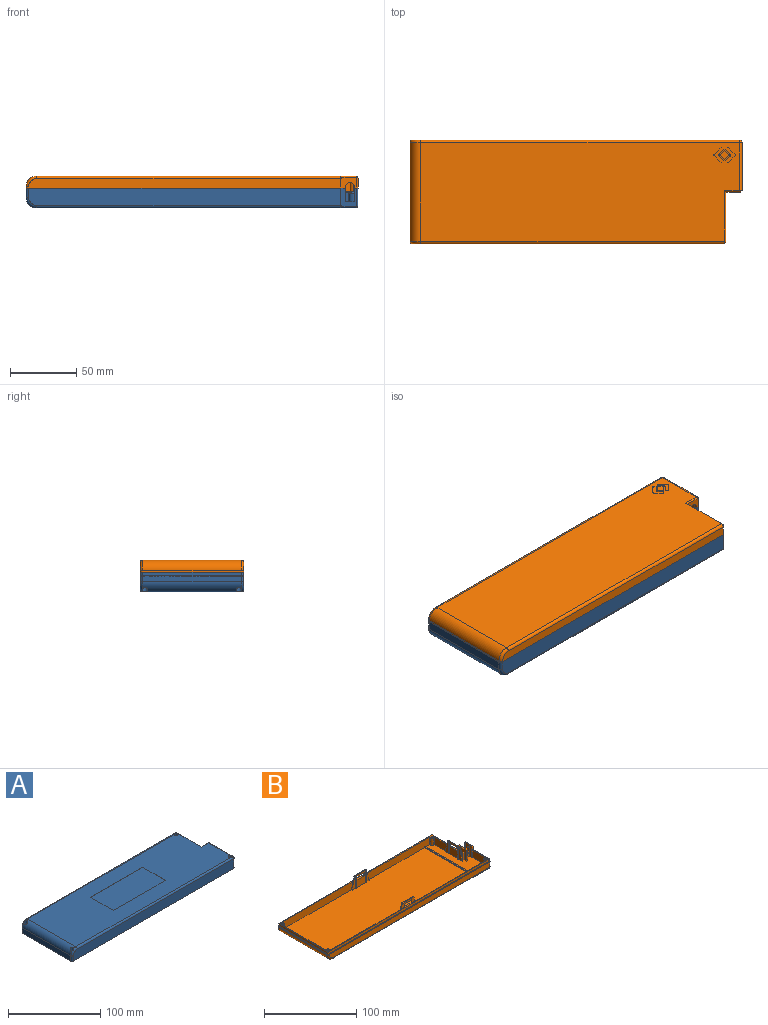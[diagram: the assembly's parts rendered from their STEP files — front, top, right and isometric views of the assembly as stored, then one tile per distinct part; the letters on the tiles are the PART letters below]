
ASSEMBLY  parts=2 mates=1
PART A: 171 faces, bbox 250.8x78.1x15.8 mm
  f0: plane 74x22.5mm, normal (0,0,-1), area 1104.2mm2, adj f1,f2,f3,f4,f12,f13,f18,f19
  f1: plane 20.61x10.11mm, normal (-1,0,0), area 193.9mm2, adj f0,f17,f131,f133,f160,f161
  f2: plane 58.61x10.11mm, normal (0,1,0), area 572.4mm2, adj f0,f17,f29,f30,f31,f40,f128,f160
  f3: plane 35.61x10.11mm, normal (-1,0,0), area 328.9mm2, adj f0,f17,f120,f148,f149,f152,f159,f162
  f4: plane 46.51x10.11mm, normal (0,-1,0), area 451.4mm2, adj f0,f17,f29,f30,f31,f60,f128,f159
  f5: plane 67.11x4.11mm, normal (1,0,0), area 259.8mm2, adj f17,f115,f157,f158,f163,f164
  f6: plane 1.5x1.29mm, normal (1,0,0), area 1.1mm2, adj f126,f147,f150,f168
  f7: plane 1.5x1.29mm, normal (-1,0,0), area 1.1mm2, adj f126,f147,f150,f168
  f8: plane 10x1.2mm, normal (0,0,1), area 12mm2, adj f9,f78,f79,f167
  f9: plane 38x10mm, normal (0,1,0), area 365mm2, adj f8,f17,f44,f54,f78,f79,f128,f151
  f10: plane 12x2mm, normal (0,0,-1), area 15.6mm2, adj f12,f15,f20,f93,f111,f131,f133,f134
  f11: plane 6x2.8mm, normal (0,0,-1), area 16.8mm2, adj f97,f98,f99,f111
  f12: plane 8x5.5mm, normal (-1,0,0), area 44mm2, adj f0,f10,f111,f170
  f13: plane 8x5.5mm, normal (1,0,0), area 44mm2, adj f0,f16,f111,f169
  f14: plane 7.5x3.6mm, normal (0,-1,0), area 22.5mm2, adj f16,f17,f88,f89,f130,f136
  f15: plane 7.5x1.6mm, normal (0,-1,0), area 12mm2, adj f10,f88,f93,f134
  f16: plane 12x3mm, normal (0,0,-1), area 27.6mm2, adj f13,f14,f18,f19,f111,f130,f132,f136
  f17: plane 248x76mm, normal (0,0,-1), area 665.4mm2, adj f1,f2,f3,f4,f5,f9,f14,f42
  f18: plane 11x5.5mm, normal (-1,0,0), area 60.5mm2, adj f0,f16,f120,f132
  f19: plane 5.5x3mm, normal (1,0,0), area 16.5mm2, adj f0,f16,f132,f169
  f20: plane 5.5x3mm, normal (-1,0,0), area 16.5mm2, adj f0,f10,f133,f170
  f21: plane 35x0.2mm, normal (1,0,0), area 7mm2, adj f22,f24,f25,f26
  f22: plane 80x0.2mm, normal (0,-1,0), area 16mm2, adj f21,f23,f25,f26
  f23: plane 35x0.2mm, normal (-1,0,0), area 7mm2, adj f22,f24,f25,f26
  f24: plane 80x0.2mm, normal (0,1,0), area 16mm2, adj f21,f23,f25,f26
  f25: plane 80x35mm, normal (0,0,1), area 2800mm2, adj f21,f22,f23,f24
  f26: plane 240x74mm, normal (0,0,1), area 14515mm2, adj f21,f22,f23,f24,f27,f28,f34,f35
  f27: cylinder r=2.05mm len=10mm, axis (0,0,1), area 128.6mm2, adj f26,f81,f100,f103,f129
  f28: cylinder r=2.05mm len=10mm, axis (0,0,1), area 128.8mm2, adj f26,f87,f105
  f29: plane 74x1.5mm, normal (0,0,-1), area 111mm2, adj f2,f4,f30,f31
  f30: plane 74x1mm, normal (-1,0,0), area 74mm2, adj f2,f4,f29,f128
  f31: plane 74x1mm, normal (1,0,0), area 74mm2, adj f0,f2,f4,f29
  f32: plane 13x1mm, normal (0.71,0.71,0), area 18.4mm2, adj f33,f88,f110,f117
  f33: cone r=1mm half-angle=45deg, axis (0,-1,0), area 3.3mm2, adj f32,f34,f100,f117
  f34: plane 11.1x1mm, normal (0,0.71,0.71), area 15mm2, adj f26,f33,f35,f117
  f35: plane 38x1mm, normal (0.71,0,0.71), area 53mm2, adj f26,f34,f36,f116
  f36: cone r=1mm half-angle=45deg, axis (-1,0,0), area 3.3mm2, adj f35,f37,f105,f116
  f37: plane 13x1mm, normal (0.71,0.71,0), area 18.4mm2, adj f36,f88,f109,f116
  f38: plane 2.25x2mm, normal (0,0,-1), area 4.5mm2, adj f39,f40,f41,f143
  f39: plane 12x2mm, normal (0,1,0), area 24mm2, adj f38,f40,f41,f128
  f40: plane 12x3mm, normal (1,0,0), area 35.7mm2, adj f2,f38,f39,f42,f128,f143
  f41: plane 12x3mm, normal (-1,0,0), area 35.7mm2, adj f38,f39,f42,f123,f128,f143
  f42: plane 2x1.25mm, normal (0,-1,0), area 2.5mm2, adj f17,f40,f41,f143
  f43: plane 2.25x2mm, normal (0,0,-1), area 4.5mm2, adj f44,f45,f46,f144
  f44: plane 12x3mm, normal (-1,0,0), area 35.7mm2, adj f9,f43,f45,f47,f128,f144
  f45: plane 12x2mm, normal (0,1,0), area 24mm2, adj f43,f44,f46,f128
  f46: plane 12x3mm, normal (1,0,0), area 35.7mm2, adj f43,f45,f47,f123,f128,f144
  f47: plane 2x1.25mm, normal (0,-1,0), area 2.5mm2, adj f17,f44,f46,f144
  f48: plane 2.25x2mm, normal (0,0,-1), area 4.5mm2, adj f49,f50,f51,f145
  f49: plane 12x3mm, normal (-1,0,0), area 35.7mm2, adj f48,f50,f52,f122,f128,f145
  f50: plane 12x2mm, normal (0,1,0), area 24mm2, adj f48,f49,f51,f128
  f51: plane 12x3mm, normal (1,0,0), area 35.7mm2, adj f48,f50,f52,f121,f128,f145
  f52: plane 2x1.25mm, normal (0,-1,0), area 2.5mm2, adj f17,f49,f51,f145
  f53: plane 2.25x2mm, normal (0,0,-1), area 4.5mm2, adj f54,f55,f56,f146
  f54: plane 12x3mm, normal (1,0,0), area 35.7mm2, adj f9,f53,f56,f57,f128,f146
  f55: plane 12x3mm, normal (-1,0,0), area 35.7mm2, adj f53,f56,f57,f121,f128,f146
  f56: plane 12x2mm, normal (0,1,0), area 24mm2, adj f53,f54,f55,f128
  f57: plane 2x1.25mm, normal (0,-1,0), area 2.5mm2, adj f17,f54,f55,f146
  f58: plane 2.25x2mm, normal (0,0,-1), area 4.5mm2, adj f59,f60,f61,f142
  f59: plane 12x3mm, normal (-1,0,0), area 35.7mm2, adj f58,f61,f62,f127,f128,f142
  f60: plane 12x3mm, normal (1,0,0), area 35.7mm2, adj f4,f58,f61,f62,f128,f142
  f61: plane 12x2mm, normal (0,-1,0), area 24mm2, adj f58,f59,f60,f128
  f62: plane 2x1.25mm, normal (0,1,0), area 2.5mm2, adj f17,f59,f60,f142
  f63: plane 2.25x2mm, normal (0,0,-1), area 4.5mm2, adj f64,f65,f66,f141
  f64: plane 12x3mm, normal (-1,0,0), area 35.7mm2, adj f63,f66,f67,f126,f128,f141
  f65: plane 12x3mm, normal (1,0,0), area 35.7mm2, adj f63,f66,f67,f127,f128,f141
  f66: plane 12x2mm, normal (0,-1,0), area 24mm2, adj f63,f64,f65,f128
  f67: plane 2x1.25mm, normal (0,1,0), area 2.5mm2, adj f17,f64,f65,f141
  f68: plane 2.25x2mm, normal (0,0,-1), area 4.5mm2, adj f69,f70,f71,f140
  f69: plane 12x3mm, normal (1,0,0), area 35.7mm2, adj f68,f70,f72,f126,f128,f140
  f70: plane 12x2mm, normal (0,-1,0), area 24mm2, adj f68,f69,f71,f128
  f71: plane 12x3mm, normal (-1,0,0), area 35.7mm2, adj f68,f70,f72,f125,f128,f140
  f72: plane 2x1.25mm, normal (0,1,0), area 2.5mm2, adj f17,f69,f71,f140
  f73: plane 2.25x2mm, normal (0,0,-1), area 4.5mm2, adj f74,f75,f76,f139
  f74: plane 12x3mm, normal (-1,0,0), area 35.7mm2, adj f73,f76,f77,f124,f128,f139
  f75: plane 12x3mm, normal (1,0,0), area 35.7mm2, adj f73,f76,f77,f125,f128,f139
  f76: plane 12x2mm, normal (0,-1,0), area 24mm2, adj f73,f74,f75,f128
  f77: plane 2x1.25mm, normal (0,1,0), area 2.5mm2, adj f17,f74,f75,f139
  f78: plane 1.5x1.29mm, normal (1,0,0), area 1.1mm2, adj f8,f9,f151,f167
  f79: plane 1.5x1.29mm, normal (-1,0,0), area 1.1mm2, adj f8,f9,f151,f167
  f80: cylinder r=1mm len=2mm, axis (0,0,-1), area 12.6mm2, adj f17,f81
  f81: plane 4.1x4.1mm, normal (0,0,1), area 10.1mm2, adj f27,f80
  f82: cylinder r=1mm len=2mm, axis (0,0,-1), area 12.6mm2, adj f17,f83
  f83: plane 4.1x4.1mm, normal (0,0,1), area 10.1mm2, adj f82,f119
  f84: cylinder r=1mm len=2mm, axis (0,0,-1), area 12.6mm2, adj f17,f85
  f85: plane 4.1x4.1mm, normal (0,0,1), area 10.1mm2, adj f84,f118
  f86: cylinder r=1mm len=2mm, axis (0,0,-1), area 12.6mm2, adj f17,f87
  f87: plane 4.1x4.1mm, normal (0,0,1), area 10.1mm2, adj f28,f86
  f88: plane 250x78mm, normal (0,0,-1), area 642.2mm2, adj f14,f15,f32,f37,f89,f90,f91,f92
  f89: plane 39x3mm, normal (-1,0,0), area 117mm2, adj f14,f17,f88,f96
  f90: cylinder r=1mm len=3mm, axis (0,0,1), area 4.7mm2, adj f17,f88,f95,f96
  f91: cylinder r=1mm len=3mm, axis (0,0,1), area 4.7mm2, adj f17,f88,f94,f95
  f92: cylinder r=1mm len=3mm, axis (0,0,1), area 4.7mm2, adj f17,f88,f93,f94
  f93: plane 36x7.5mm, normal (-1,0,0), area 158mm2, adj f10,f15,f17,f88,f92,f131,f153,f154
  f94: plane 246x3mm, normal (0,1,0), area 738mm2, adj f17,f88,f91,f92
  f95: plane 74x3mm, normal (1,0,0), area 222mm2, adj f17,f88,f90,f91
  f96: plane 234.9x3mm, normal (0,-1,0), area 704.7mm2, adj f17,f88,f89,f90
  f97: plane 6x2.18mm, normal (1,0,0), area 13mm2, adj f0,f11,f98,f111
  f98: plane 2.8x2.18mm, normal (0,-1,0), area 6.1mm2, adj f0,f11,f97,f99
  f99: plane 6x2.18mm, normal (-1,0,0), area 13mm2, adj f0,f11,f98,f111
  f100: cylinder r=2mm len=36mm, axis (0,1,0), area 112mm2, adj f26,f27,f33,f101,f110,f129
  f101: sphere r=2mm, area 6.3mm2, adj f100,f103,f112
  f102: torus R=6mm, axis (0,1,0), area 34.6mm2, adj f103,f106,f107,f113,f119
  f103: cylinder r=2mm len=240mm, axis (1,0,0), area 752.9mm2, adj f26,f27,f101,f102,f107,f129
  f104: torus R=6mm, axis (0,1,0), area 34.6mm2, adj f105,f106,f109,f114,f118
  f105: cylinder r=2mm len=228.9mm, axis (-1,0,0), area 718mm2, adj f26,f28,f36,f104,f109
  f106: cylinder r=8mm len=74mm, axis (0,-1,0), area 899.5mm2, adj f26,f102,f104,f108,f118,f119
  f107: plane 246x13mm, normal (0,-1,0), area 3190.3mm2, adj f88,f102,f103,f112,f113
  f108: plane 74x7mm, normal (-1,0,0), area 518mm2, adj f88,f106,f113,f114
  f109: plane 234.9x13mm, normal (0,1,0), area 3046mm2, adj f37,f88,f104,f105,f114
  f110: plane 36x13mm, normal (1,0,0), area 468mm2, adj f32,f88,f100,f112
  f111: plane 8.1x5.5mm, normal (0,-1,0), area 19.7mm2, adj f0,f10,f11,f12,f13,f16,f97,f99
  f112: cylinder r=2mm len=13mm, axis (0,0,-1), area 40.8mm2, adj f88,f101,f107,f110
  f113: cylinder r=2mm len=7mm, axis (0,0,1), area 22mm2, adj f88,f102,f107,f108
  f114: cylinder r=2mm len=7mm, axis (0,0,-1), area 22mm2, adj f88,f104,f108,f109
  f115: cylinder r=6mm len=74mm, axis (0,-1,0), area 620.7mm2, adj f5,f122,f124,f128,f157,f158
  f116: plane 38x14mm, normal (1,0,0), area 531.8mm2, adj f35,f36,f37,f88,f117
  f117: plane 14x11.1mm, normal (0,1,0), area 84.7mm2, adj f32,f33,f34,f88,f116,f134,f135,f136
  f118: cylinder r=2.05mm len=9.62mm, axis (0,0,-1), area 107.2mm2, adj f85,f104,f106
  f119: cylinder r=2.05mm len=9.62mm, axis (0,0,-1), area 107.2mm2, adj f83,f102,f106
  f120: plane 10x3.29mm, normal (0,-1,0), area 21.1mm2, adj f0,f3,f17,f18,f130,f148,f152,f165
  f121: plane 38x10mm, normal (0,1,0), area 380mm2, adj f17,f51,f55,f128
  f122: plane 58.61x10.11mm, normal (0,1,0), area 573.9mm2, adj f17,f49,f115,f128,f157,f164
  f123: plane 38x10mm, normal (0,1,0), area 380mm2, adj f17,f41,f46,f128
  f124: plane 58.61x10.11mm, normal (0,-1,0), area 573.9mm2, adj f17,f74,f115,f128,f158,f163
  f125: plane 38x10mm, normal (0,-1,0), area 380mm2, adj f17,f71,f75,f128
  f126: plane 38x10mm, normal (0,-1,0), area 365mm2, adj f6,f7,f17,f64,f69,f128,f147,f150
  f127: plane 38x10mm, normal (0,-1,0), area 380mm2, adj f17,f59,f65,f128
  f128: plane 216x74mm, normal (0,0,-1), area 15936mm2, adj f2,f4,f9,f30,f39,f40,f41,f44
  f129: plane 0.1x0.1mm, normal (0,0,1), area 0mm2, adj f27,f100,f103
  f130: plane 4.5x1mm, normal (1,0,0), area 4.5mm2, adj f14,f16,f17,f120
  f131: plane 4.5x1mm, normal (0,1,0), area 4.5mm2, adj f1,f10,f17,f93
  f132: plane 5.5x3mm, normal (0,-1,0), area 16.5mm2, adj f0,f16,f18,f19
  f133: plane 5.5x1mm, normal (0,-1,0), area 5.5mm2, adj f0,f1,f10,f20
  f134: plane 9.83x2mm, normal (-1,0,0), area 12.2mm2, adj f10,f15,f88,f111,f117,f137
  f135: plane 6.1x2mm, normal (0,0,-1), area 12.2mm2, adj f111,f117,f137,f138
  f136: plane 9.83x2mm, normal (1,0,0), area 12.2mm2, adj f14,f16,f88,f111,f117,f138
  f137: cylinder r=0.4mm len=2mm, axis (0,-1,0), area 1.3mm2, adj f111,f117,f134,f135
  f138: cylinder r=0.4mm len=2mm, axis (0,1,0), area 1.3mm2, adj f111,f117,f135,f136
  f139: plane 2x0.75mm, normal (0,0.71,-0.71), area 2.1mm2, adj f73,f74,f75,f77
  f140: plane 2x0.75mm, normal (0,0.71,-0.71), area 2.1mm2, adj f68,f69,f71,f72
  f141: plane 2x0.75mm, normal (0,0.71,-0.71), area 2.1mm2, adj f63,f64,f65,f67
  f142: plane 2x0.75mm, normal (0,0.71,-0.71), area 2.1mm2, adj f58,f59,f60,f62
  f143: plane 2x0.75mm, normal (0,-0.71,-0.71), area 2.1mm2, adj f38,f40,f41,f42
  f144: plane 2x0.75mm, normal (0,-0.71,-0.71), area 2.1mm2, adj f43,f44,f46,f47
  f145: plane 2x0.75mm, normal (0,-0.71,-0.71), area 2.1mm2, adj f48,f49,f51,f52
  f146: plane 2x0.75mm, normal (0,-0.71,-0.71), area 2.1mm2, adj f53,f54,f55,f57
  f147: plane 10x1.2mm, normal (0,0,1), area 12mm2, adj f6,f7,f126,f168
  f148: plane 10x1.2mm, normal (0,0,1), area 12mm2, adj f3,f120,f149,f165
  f149: plane 1.5x1.29mm, normal (0,1,0), area 1.1mm2, adj f3,f148,f152,f165
  f150: plane 10x1.29mm, normal (0,-0.71,-0.71), area 18.2mm2, adj f6,f7,f126,f168
  f151: plane 10x1.29mm, normal (0,0.71,-0.71), area 18.2mm2, adj f9,f78,f79,f167
  f152: plane 10x1.29mm, normal (-0.71,0,-0.71), area 18.2mm2, adj f3,f120,f149,f165
  f153: plane 1x0.79mm, normal (0,-1,0), area 0.5mm2, adj f93,f154,f156,f166
  f154: plane 4x0.7mm, normal (0,0,1), area 2.8mm2, adj f93,f153,f155,f166
  f155: plane 1x0.79mm, normal (0,1,0), area 0.5mm2, adj f93,f154,f156,f166
  f156: plane 4x0.79mm, normal (-0.71,0,-0.71), area 4.5mm2, adj f93,f153,f155,f166
  f157: cylinder r=3.5mm len=8.92mm, axis (0,0,-1), area 68.9mm2, adj f5,f115,f122,f164
  f158: cylinder r=3.5mm len=8.92mm, axis (0,0,-1), area 68.9mm2, adj f5,f115,f124,f163
  f159: cylinder r=3.5mm len=9mm, axis (0,0,-1), area 77.4mm2, adj f0,f3,f4,f162
  f160: cylinder r=3.5mm len=9mm, axis (0,0,-1), area 77.4mm2, adj f0,f1,f2,f161
  f161: cone r=2.5mm half-angle=45deg, axis (0,0,1), area 11.2mm2, adj f1,f2,f17,f160
  f162: cone r=2.5mm half-angle=45deg, axis (0,0,1), area 11.2mm2, adj f3,f4,f17,f159
  f163: cone r=2.5mm half-angle=45deg, axis (0,0,1), area 11.2mm2, adj f5,f17,f124,f158
  f164: cone r=2.5mm half-angle=45deg, axis (0,0,1), area 11.2mm2, adj f5,f17,f122,f157
  f165: plane 10x0.21mm, normal (-0.92,0,0.38), area 2.3mm2, adj f120,f148,f149,f152
  f166: plane 4x0.21mm, normal (-0.92,0,0.38), area 0.9mm2, adj f153,f154,f155,f156
  f167: plane 10x0.21mm, normal (0,0.92,0.38), area 2.3mm2, adj f8,f78,f79,f151
  f168: plane 10x0.21mm, normal (0,-0.92,0.38), area 2.3mm2, adj f6,f7,f147,f150
  f169: plane 5.5x1mm, normal (0,1,0), area 5.5mm2, adj f0,f13,f16,f19
  f170: plane 5.5x1mm, normal (0,1,0), area 5.5mm2, adj f0,f10,f12,f20
PART B: 196 faces, bbox 250.7x78x19.2 mm
  f0: plane 14.5x8mm, normal (-1,0,0), area 96.6mm2, adj f7,f100,f124,f126,f127,f128,f131,f143
  f1: plane 16.5x5mm, normal (-1,0,0), area 49.5mm2, adj f7,f142,f154,f180
  f2: plane 16.5x14mm, normal (-1,0,0), area 184.8mm2, adj f7,f23,f67,f68,f142,f162,f178,f181
  f3: plane 16.5x13.95mm, normal (0,1,0), area 183.9mm2, adj f20,f23,f69,f70,f140,f160,f172,f175
  f4: plane 16.5x5mm, normal (0,1,0), area 49.5mm2, adj f20,f140,f159,f171
  f5: plane 16.5x5mm, normal (0,-1,0), area 49.5mm2, adj f20,f141,f156,f168
  f6: plane 16.5x14mm, normal (0,-1,0), area 184.8mm2, adj f20,f23,f71,f72,f141,f161,f166,f169
  f7: plane 74x22.5mm, normal (0,0,1), area 1045.7mm2, adj f0,f1,f2,f8,f14,f16,f56,f75
  f8: plane 14.5x8mm, normal (1,0,0), area 105.4mm2, adj f7,f65,f66,f100,f125,f127,f130,f163
  f9: plane 21.15x6.5mm, normal (1,0,0), area 81mm2, adj f23,f67,f68,f142,f154,f155,f162
  f10: plane 21.15x6.5mm, normal (0,-1,0), area 81mm2, adj f23,f69,f70,f140,f158,f159,f160
  f11: plane 16.5x5mm, normal (0,-1,0), area 49.5mm2, adj f20,f141,f157,f165
  f12: plane 16.5x5.05mm, normal (0,1,0), area 50.4mm2, adj f20,f140,f158,f174
  f13: plane 108.42x10mm, normal (0,-1,0), area 1071.9mm2, adj f20,f23,f84,f117,f157
  f14: plane 96.32x10mm, normal (0,-1,0), area 949.6mm2, adj f7,f20,f23,f54,f55,f56,f76,f156
  f15: plane 2.71x1.5mm, normal (0,0,1), area 4.1mm2, adj f16,f17,f73,f152
  f16: plane 14.5x12mm, normal (-1,0,0), area 141.1mm2, adj f7,f15,f18,f23,f73,f96,f121,f130
  f17: plane 10x2.71mm, normal (1,0,0), area 27.1mm2, adj f15,f23,f73,f152
  f18: plane 3x1.5mm, normal (0,0,1), area 4.5mm2, adj f16,f19,f151,f153
  f19: plane 10x3mm, normal (1,0,0), area 30mm2, adj f18,f23,f151,f153
  f20: plane 216x74mm, normal (0,0,1), area 15930mm2, adj f3,f4,f5,f6,f11,f12,f13,f14
  f21: plane 108.42x10mm, normal (0,1,0), area 1071.9mm2, adj f20,f23,f83,f117,f158
  f22: plane 21.15x6.5mm, normal (0,1,0), area 81mm2, adj f23,f71,f72,f141,f156,f157,f161
  f23: plane 248x76mm, normal (0,0,1), area 708.2mm2, adj f2,f3,f6,f9,f10,f13,f14,f16
  f24: plane 3.2x3.19mm, normal (-0.71,-0.71,0), area 1.4mm2, adj f25,f29,f30,f31
  f25: plane 3.14x3.12mm, normal (0.71,-0.71,0), area 1.3mm2, adj f24,f26,f30,f31
  f26: cylinder r=0.54mm len=0.77mm, axis (0,0,1), area 0.3mm2, adj f25,f27,f30,f31
  f27: plane 3.17x3.15mm, normal (0.71,0.71,0), area 1.3mm2, adj f26,f28,f30,f31
  f28: plane 3.15x3.14mm, normal (-0.71,0.71,0), area 1.3mm2, adj f27,f29,f30,f31
  f29: cylinder r=0.52mm len=0.71mm, axis (0,0,1), area 0.2mm2, adj f24,f28,f30,f31
  f30: plane 7.06x6.62mm, normal (0,0,-1), area 24.8mm2, adj f24,f25,f26,f27,f28,f29
  f31: plane 240x74mm, normal (0,0,-1), area 17244mm2, adj f24,f25,f26,f27,f28,f29,f32,f33
  f32: cylinder r=0.43mm len=0.63mm, axis (0,0,1), area 0.2mm2, adj f31,f33,f41,f42
  f33: plane 5.2x5.19mm, normal (0.71,-0.71,0), area 2.2mm2, adj f31,f32,f34,f42
  f34: cylinder r=0.55mm len=0.79mm, axis (0,0,1), area 0.3mm2, adj f31,f33,f35,f42
  f35: plane 5.24x5.22mm, normal (0.71,0.71,0), area 2.2mm2, adj f31,f34,f36,f42
  f36: cylinder r=0.43mm len=0.61mm, axis (0,0,1), area 0.2mm2, adj f31,f35,f37,f42
  f37: plane 1.41x1.41mm, normal (-0.71,0.71,0), area 0.6mm2, adj f31,f36,f38,f42
  f38: plane 3.23x3.22mm, normal (-0.71,-0.71,0), area 1.4mm2, adj f31,f37,f39,f42
  f39: cylinder r=1.41mm len=1.99mm, axis (0,0,1), area 0.7mm2, adj f31,f38,f40,f42
  f40: plane 3.2x3.19mm, normal (-0.71,0.71,0), area 1.4mm2, adj f31,f39,f41,f42
  f41: plane 1.4x1.4mm, normal (-0.71,-0.71,0), area 0.6mm2, adj f31,f32,f40,f42
  f42: plane 11.48x7.42mm, normal (0,0,-1), area 34.9mm2, adj f32,f33,f34,f35,f36,f37,f38,f39
  f43: plane 3.23x3.22mm, normal (0.71,0.71,0), area 1.4mm2, adj f31,f44,f52,f53
  f44: cylinder r=1.41mm len=2mm, axis (0,0,1), area 0.7mm2, adj f31,f43,f45,f53
  f45: plane 3.22x3.21mm, normal (0.71,-0.71,0), area 1.4mm2, adj f31,f44,f46,f53
  f46: plane 1.34x1.33mm, normal (0.71,0.71,0), area 0.6mm2, adj f31,f45,f47,f53
  f47: cylinder r=0.51mm len=0.72mm, axis (0,0,1), area 0.2mm2, adj f31,f46,f48,f53
  f48: plane 5.19x5.16mm, normal (-0.71,0.71,0), area 2.2mm2, adj f31,f47,f49,f53
  f49: cylinder r=0.53mm len=0.75mm, axis (0,0,1), area 0.2mm2, adj f31,f48,f50,f53
  f50: plane 5.2x5.18mm, normal (-0.71,-0.71,0), area 2.2mm2, adj f31,f49,f51,f53
  f51: cylinder r=0.53mm len=0.79mm, axis (0,0,1), area 0.3mm2, adj f31,f50,f52,f53
  f52: plane 1.27x1.26mm, normal (0.71,-0.71,0), area 0.5mm2, adj f31,f43,f51,f53
  f53: plane 11.39x7.4mm, normal (0,0,-1), area 34.5mm2, adj f43,f44,f45,f46,f47,f48,f49,f50
  f54: plane 74x1.5mm, normal (0,0,1), area 111mm2, adj f14,f55,f56,f129
  f55: plane 74x1mm, normal (-1,0,0), area 74mm2, adj f14,f20,f54,f129
  f56: plane 74x1mm, normal (1,0,0), area 74mm2, adj f7,f14,f54,f129
  f57: plane 7x1mm, normal (0.71,0.71,0), area 9.9mm2, adj f58,f87,f110,f115
  f58: cone r=2mm half-angle=45deg, axis (-1,0,0), area 3.3mm2, adj f57,f59,f106,f115
  f59: plane 38x1mm, normal (0.71,0,-0.71), area 53mm2, adj f31,f58,f60,f115
  f60: plane 11.1x1mm, normal (0,0.71,-0.71), area 15mm2, adj f31,f59,f61,f116
  f61: cone r=2mm half-angle=45deg, axis (0,-1,0), area 3.3mm2, adj f60,f62,f101,f116
  f62: plane 7x1mm, normal (0.71,0.71,0), area 9.9mm2, adj f61,f87,f111,f116
  f63: plane 4x2mm, normal (1,0,0), area 8mm2, adj f123,f126,f127,f128
  f64: plane 4x2mm, normal (-1,0,0), area 8mm2, adj f65,f66,f123,f127
  f65: plane 4x2.65mm, normal (0,0,1), area 10.6mm2, adj f8,f64,f66,f127
  f66: plane 4.8x2.65mm, normal (0,1,0), area 9mm2, adj f8,f64,f65,f125
  f67: plane 4.2x1mm, normal (0,-1,0), area 4.2mm2, adj f2,f9,f23,f162
  f68: plane 4.2x1mm, normal (0,1,0), area 4.2mm2, adj f2,f9,f23,f162
  f69: plane 4.2x1mm, normal (1,0,0), area 4.2mm2, adj f3,f10,f23,f160
  f70: plane 4.2x1mm, normal (-1,0,0), area 4.2mm2, adj f3,f10,f23,f160
  f71: plane 4.2x1mm, normal (-1,0,0), area 4.2mm2, adj f6,f22,f23,f161
  f72: plane 4.2x1mm, normal (1,0,0), area 4.2mm2, adj f6,f22,f23,f161
  f73: plane 10x1.5mm, normal (0,-1,0), area 15mm2, adj f15,f16,f17,f23
  f74: plane 10x2.42mm, normal (-1,0,0), area 12.1mm2, adj f23,f121,f154
  f75: cylinder r=2.5mm len=10mm, axis (0,0,1), area 39.3mm2, adj f7,f23,f76,f77
  f76: plane 10x1.5mm, normal (-1,0,0), area 15mm2, adj f7,f14,f23,f75
  f77: plane 10x1.5mm, normal (0,-1,0), area 15mm2, adj f7,f23,f75,f120
  f78: cylinder r=2.5mm len=10mm, axis (0,0,1), area 39.3mm2, adj f7,f23,f79,f80
  f79: plane 10x1.5mm, normal (0,1,0), area 15mm2, adj f7,f23,f78,f119
  f80: plane 10x1.5mm, normal (-1,0,0), area 15mm2, adj f7,f23,f78,f129
  f81: plane 7.97x1.5mm, normal (0,1,0), area 10.1mm2, adj f23,f82,f117,f118
  f82: cylinder r=2.5mm len=9.66mm, axis (0,0,1), area 36mm2, adj f23,f81,f83,f117
  f83: plane 9.66x1.5mm, normal (1,0,0), area 14.5mm2, adj f21,f23,f82,f117
  f84: plane 9.66x1.5mm, normal (1,0,0), area 14.5mm2, adj f13,f23,f85,f117
  f85: cylinder r=2.5mm len=9.66mm, axis (0,0,1), area 36mm2, adj f23,f84,f86,f117
  f86: plane 7.97x1.5mm, normal (0,-1,0), area 10.1mm2, adj f23,f85,f117,f118
  f87: plane 250x78mm, normal (0,0,1), area 642.2mm2, adj f57,f62,f88,f89,f90,f91,f92,f93
  f88: plane 35.9x7.4mm, normal (1,0,0), area 150.9mm2, adj f23,f87,f89,f143,f144,f145,f146,f147
  f89: cylinder r=1mm len=3mm, axis (0,0,1), area 4.7mm2, adj f23,f87,f88,f90
  f90: plane 246x3mm, normal (0,-1,0), area 738mm2, adj f23,f87,f89,f91
  f91: cylinder r=1mm len=3mm, axis (0,0,1), area 4.7mm2, adj f23,f87,f90,f92
  f92: plane 74x3mm, normal (-1,0,0), area 222mm2, adj f23,f87,f91,f93
  f93: cylinder r=1mm len=3mm, axis (0,0,1), area 4.7mm2, adj f23,f87,f92,f94
  f94: plane 234.7x3mm, normal (0,1,0), area 704.1mm2, adj f23,f87,f93,f139
  f95: plane 38.8x3mm, normal (1,0,0), area 116.4mm2, adj f23,f87,f96,f139
  f96: plane 7.5x3.6mm, normal (0,1,0), area 20.3mm2, adj f16,f23,f87,f95,f130,f134
  f97: plane 7.5x1.5mm, normal (0,1,0), area 11.3mm2, adj f87,f131,f138,f146
  f98: plane 14.5x3mm, normal (1,0,0), area 43.5mm2, adj f7,f130,f133,f163
  f99: plane 14.5x3mm, normal (-1,0,0), area 43.5mm2, adj f7,f131,f132,f149,f164
  f100: plane 8.1x4.98mm, normal (0,-1,0), area 25mm2, adj f0,f7,f8,f123,f124,f125
  f101: cylinder r=2mm len=36mm, axis (0,1,0), area 113.1mm2, adj f31,f61,f102,f111
  f102: sphere r=2mm, area 6.3mm2, adj f101,f104,f112
  f103: torus R=6mm, axis (0,1,0), area 35.9mm2, adj f104,f107,f108,f113
  f104: cylinder r=2mm len=240mm, axis (1,0,0), area 754mm2, adj f31,f102,f103,f108
  f105: torus R=6mm, axis (0,1,0), area 35.9mm2, adj f106,f107,f110,f114
  f106: cylinder r=2mm len=228.9mm, axis (-1,0,0), area 719.1mm2, adj f31,f58,f105,f110
  f107: cylinder r=8mm len=74mm, axis (0,-1,0), area 929.9mm2, adj f31,f103,f105,f109
  f108: plane 246x7mm, normal (0,-1,0), area 1714.3mm2, adj f87,f103,f104,f112,f113
  f109: plane 74x1mm, normal (-1,0,0), area 74mm2, adj f87,f107,f113,f114
  f110: plane 234.9x7mm, normal (0,1,0), area 1636.6mm2, adj f57,f87,f105,f106,f114
  f111: plane 36x7mm, normal (1,0,0), area 252mm2, adj f62,f87,f101,f112
  f112: cylinder r=2mm len=7mm, axis (0,0,1), area 22mm2, adj f87,f102,f108,f111
  f113: cylinder r=2mm len=2mm, axis (0,0,-1), area 3.1mm2, adj f87,f103,f108,f109
  f114: cylinder r=2mm len=2mm, axis (0,0,1), area 3.1mm2, adj f87,f105,f109,f110
  f115: plane 38x8mm, normal (1,0,0), area 303.8mm2, adj f57,f58,f59,f87,f116
  f116: plane 11.1x8mm, normal (0,1,0), area 65.1mm2, adj f60,f61,f62,f87,f115,f134,f135,f136
  f117: cylinder r=6mm len=74mm, axis (0,-1,0), area 641.3mm2, adj f13,f20,f21,f81,f82,f83,f84,f85
  f118: plane 66x4mm, normal (1,0,0), area 264mm2, adj f23,f81,f86,f117
  f119: plane 20x10mm, normal (-1,0,0), area 200mm2, adj f7,f23,f79,f132
  f120: plane 19.42x10mm, normal (-1,0,0), area 182.1mm2, adj f7,f23,f77,f155
  f121: plane 10x2.5mm, normal (0,-1,0), area 25mm2, adj f7,f16,f23,f74
  f122: plane 16.5x5mm, normal (-1,0,0), area 49.5mm2, adj f7,f142,f155,f177
  f123: plane 6x2.8mm, normal (0,0,1), area 16.8mm2, adj f63,f64,f100,f124,f125,f127
  f124: plane 2.8x2.65mm, normal (-0.73,0,0.69), area 7.7mm2, adj f0,f100,f123,f128
  f125: plane 2.8x2.65mm, normal (0.73,0,0.69), area 7.7mm2, adj f8,f66,f100,f123
  f126: plane 4x2.65mm, normal (0,0,1), area 10.6mm2, adj f0,f63,f127,f128
  f127: plane 14.33x8.1mm, normal (0,-1,0), area 35.2mm2, adj f0,f8,f63,f64,f65,f123,f126,f130
  f128: plane 4.8x2.65mm, normal (0,1,0), area 9mm2, adj f0,f63,f124,f126
  f129: plane 108.42x10mm, normal (0,1,0), area 1070.6mm2, adj f7,f20,f23,f54,f55,f56,f80,f159
  f130: plane 12x2.5mm, normal (0,0,1), area 21.6mm2, adj f8,f16,f96,f98,f127,f133,f134,f163
  f131: plane 11.9x1.9mm, normal (0,0,1), area 14.2mm2, adj f0,f97,f99,f127,f138,f147,f149,f164
  f132: plane 14.4x1.9mm, normal (0,-1,0), area 18.4mm2, adj f7,f23,f99,f119,f148,f149
  f133: plane 14.5x2.5mm, normal (0,-1,0), area 36.3mm2, adj f7,f16,f98,f130
  f134: plane 9.29x2mm, normal (1,0,0), area 11.1mm2, adj f87,f96,f116,f127,f130,f135
  f135: plane 2.44x2.31mm, normal (0.73,0,0.69), area 6.7mm2, adj f116,f127,f134,f136
  f136: plane 2.28x2mm, normal (0,0,1), area 4.6mm2, adj f116,f127,f135,f137
  f137: plane 2.44x2.31mm, normal (-0.73,0,0.69), area 6.7mm2, adj f116,f127,f136,f138
  f138: plane 9.29x2mm, normal (-1,0,0), area 11.1mm2, adj f87,f97,f116,f127,f131,f137
  f139: plane 3x0.2mm, normal (0.71,0.71,0), area 0.8mm2, adj f23,f87,f94,f95
  f140: plane 18x1.5mm, normal (0,0,1), area 19mm2, adj f3,f4,f10,f12,f158,f159,f171,f172
  f141: plane 18x1.5mm, normal (0,0,1), area 19mm2, adj f5,f6,f11,f22,f156,f157,f165,f166
  f142: plane 18x1.5mm, normal (0,0,1), area 19mm2, adj f1,f2,f9,f122,f154,f155,f177,f178
  f143: plane 1.75x1mm, normal (0,1,0), area 1.8mm2, adj f0,f88,f144,f195
  f144: plane 5x1mm, normal (0,0,1), area 5mm2, adj f0,f88,f143,f145
  f145: plane 1.75x1mm, normal (0,-1,0), area 1.8mm2, adj f0,f88,f144,f195
  f146: cylinder r=0.1mm len=7.5mm, axis (0,0,-1), area 1.2mm2, adj f87,f88,f97,f147
  f147: cylinder r=0.1mm len=11.9mm, axis (0,-1,0), area 1.9mm2, adj f88,f131,f146,f150
  f148: cylinder r=0.1mm len=4.4mm, axis (0,0,1), area 0.7mm2, adj f23,f88,f132,f150
  f149: cylinder r=0.1mm len=1.9mm, axis (1,0,0), area 0.3mm2, adj f99,f131,f132,f150
  f150: sphere r=0.1mm, area 0mm2, adj f147,f148,f149
  f151: plane 10x1.5mm, normal (0,1,0), area 15mm2, adj f16,f18,f19,f23
  f152: plane 10x1.5mm, normal (0,1,0), area 15mm2, adj f15,f16,f17,f23
  f153: plane 10x1.5mm, normal (0,-1,0), area 15mm2, adj f16,f18,f19,f23
  f154: plane 16.5x4mm, normal (0,-0.97,0.24), area 17mm2, adj f1,f7,f9,f74,f142
  f155: plane 16.5x4mm, normal (0,0.97,0.24), area 17mm2, adj f7,f9,f120,f122,f142
  f156: plane 16.5x4mm, normal (0.97,0,0.24), area 17mm2, adj f5,f14,f20,f22,f141
  f157: plane 16.5x4mm, normal (-0.97,0,0.24), area 17mm2, adj f11,f13,f20,f22,f141
  f158: plane 16.5x4mm, normal (-0.97,0,0.24), area 17mm2, adj f10,f12,f20,f21,f140
  f159: plane 16.5x4mm, normal (0.97,0,0.24), area 17mm2, adj f4,f10,f20,f129,f140
  f160: plane 11x1mm, normal (0,0,-1), area 11mm2, adj f3,f10,f69,f70
  f161: plane 11x1mm, normal (0,0,-1), area 11mm2, adj f6,f22,f71,f72
  f162: plane 11x1mm, normal (0,0,-1), area 11mm2, adj f2,f9,f67,f68
  f163: plane 14.5x1mm, normal (0,1,0), area 14.5mm2, adj f7,f8,f98,f130
  f164: plane 14.5x1mm, normal (0,1,0), area 14.5mm2, adj f0,f7,f99,f131
  f165: plane 16.5x0.5mm, normal (-1,0,0), area 8.3mm2, adj f11,f20,f141,f167
  f166: plane 16.5x0.5mm, normal (1,0,0), area 8.3mm2, adj f6,f20,f141,f167
  f167: plane 16.5x1mm, normal (0,-1,0), area 16.5mm2, adj f20,f141,f165,f166
  f168: plane 16.5x0.5mm, normal (1,0,0), area 8.3mm2, adj f5,f20,f141,f170
  f169: plane 16.5x0.5mm, normal (-1,0,0), area 8.3mm2, adj f6,f20,f141,f170
  f170: plane 16.5x1mm, normal (0,-1,0), area 16.5mm2, adj f20,f141,f168,f169
  f171: plane 16.5x0.5mm, normal (1,0,0), area 8.3mm2, adj f4,f20,f140,f173
  f172: plane 16.5x0.5mm, normal (-1,0,0), area 8.3mm2, adj f3,f20,f140,f173
  f173: plane 16.5x1mm, normal (0,1,0), area 16.5mm2, adj f20,f140,f171,f172
  f174: plane 16.5x0.5mm, normal (-1,0,0), area 8.3mm2, adj f12,f20,f140,f176
  f175: plane 16.5x0.5mm, normal (1,0,0), area 8.3mm2, adj f3,f20,f140,f176
  f176: plane 16.5x1mm, normal (0,1,0), area 16.5mm2, adj f20,f140,f174,f175
  f177: plane 16.5x0.5mm, normal (0,1,0), area 8.3mm2, adj f7,f122,f142,f179
  f178: plane 16.5x0.5mm, normal (0,-1,0), area 8.3mm2, adj f2,f7,f142,f179
  f179: plane 16.5x1mm, normal (-1,0,0), area 16.5mm2, adj f7,f142,f177,f178
  f180: plane 16.5x0.5mm, normal (0,-1,0), area 8.3mm2, adj f1,f7,f142,f182
  f181: plane 16.5x0.5mm, normal (0,1,0), area 8.3mm2, adj f2,f7,f142,f182
  f182: plane 16.5x1mm, normal (-1,0,0), area 16.5mm2, adj f7,f142,f180,f181
  f183: cylinder r=1.15mm len=7mm, axis (0,0,1), area 50.6mm2, adj f23,f194
  f184: cylinder r=1.15mm len=7mm, axis (0,0,1), area 50.6mm2, adj f23,f191
  f185: cylinder r=1.15mm len=7mm, axis (0,0,1), area 50.6mm2, adj f23,f192
  f186: cylinder r=1.15mm len=7mm, axis (0,0,1), area 50.6mm2, adj f23,f193
  f187: plane 0.3x0.3mm, normal (0,0,1), area 0.1mm2, adj f194
  f188: plane 0.3x0.3mm, normal (0,0,1), area 0.1mm2, adj f191
  f189: plane 0.3x0.3mm, normal (0,0,1), area 0.1mm2, adj f192
  f190: plane 0.3x0.3mm, normal (0,0,1), area 0.1mm2, adj f193
  f191: cone r=0.15mm half-angle=45deg, axis (0,0,1), area 5.8mm2, adj f184,f188
  f192: cone r=0.15mm half-angle=45deg, axis (0,0,1), area 5.8mm2, adj f185,f189
  f193: cone r=0.15mm half-angle=45deg, axis (0,0,1), area 5.8mm2, adj f186,f190
  f194: cone r=0.15mm half-angle=45deg, axis (0,0,1), area 5.8mm2, adj f183,f187
  f195: plane 5x1mm, normal (0,0,-1), area 5mm2, adj f0,f88,f143,f145
PLACE A rot(axis=(1,0,0),180deg) t=(-131.49,-52.56,-121.91)mm
PLACE B rot(axis=(1,0,0),180deg) t=(-131.49,-52.56,-97.91)mm
MATE planar B.f109 <-> A.f108  axis (-1,0,0) through (-256.49,-52.56,-106.41)mm
